# Revit family: QF_ELECTROLUXPROFESSIONAL_Professional_371329_E7IIMIAOMEA
name_source: partatom
category: Specialty Equipment
revit_build: Autodesk Revit 2018 (Build: 20190510_1515(x64)
units: mm (PartAtom-declared; Revit-internal decimal feet)

## family parameters
Always vertical = Yes
Cut with Voids When Loaded = No
Part Type = Normal
Room Calculation Point = No
Round Connector Dimension = Use Diameter
Shared = No
Work Plane-Based = No

## types (1)
- QF_ELECTROLUXPROFESSIONAL_Professional_371329_E7IIMIAOMEA
    Apparent Power = 7800 VA
    Conn Conduit = Yes
    Depth = 730 mm
    Description = 700XP Full Module Electricl Fry Top, 2/3 Smooth - 1/3 Ribbed Plate, Mild Steel - 230V
    Direct Waste Size = 0"
    FL Amps = 20 A
    HP = 10.5 HP
    Height = 291 mm
    Manufacturer = ELECTROLUX
    Max Overcurrent Protection = 0 A
    Min Ckt Ampacity = 0 A
    Model = 371200
    Phase = 3
    URL = www.electrolux.com/foodservice
    URL Cutsheet = www.electrolux.com/foodservice
    Volts = 230 V
    Watts = 7800 W
    Weight in Pounds = 185
    Width = 800 mm

## geometry (parser evidence)
native form markers: Blend x37, Sweep x2
no freeform markers — native parametric forms only
